# Revit family: TMS-Luna-Pendant
name_source: partatom
category: Lighting Fixtures
units: mm (PartAtom-declared; Revit-internal decimal feet)

## family parameters
Cut with Voids When Loaded = No
Host = Face
Light Source = No
Part Type = Normal
Room Calculation Point = No
Round Connector Dimension = Use Diameter
Shared = No

## types (18) — shared parameters
Apparent Load = 0 VA
Assembly Code = D5020200
Cable Material = Steel ASTM A53
Canopy Diameter = 0' - 10"
Canopy Material = TMS Gloss Black
Default Elevation = 4' - 0"
Fixture Material = TMS Gloss Black
Lens Material = TMS Lens
Manufacturer = TMS Lighting Inc.
Model = LUNA PENDANT
Number of Poles = 1
Power Factor = 1
URL = https://tmslighting.com
Voltage = 0 V

## per-type parameters (varying)
| type | Fixture Type | Number of Supports | Radius |
| 24" Direct | Luna-Fixture : 24" | 3 | 0' - 11 1/2" |
| 36" Direct | Luna-Fixture : 36" | 3 | 1' - 5 1/2" |
| 48" Direct | Luna-Fixture : 48" | 3 | 1' - 11 1/2" |
| 60" Direct | Luna-Fixture : 60" | 3 | 2' - 5 1/2" |
| 72" Direct | Luna-Fixture : 72" | 4 | 2' - 11 1/2" |
| 84" Direct | Luna-Fixture : 84" | 4 | 3' - 5 1/2" |
| 24" Direct/Indirect | Luna-Fixture-Dir-Ind : 24" | 3 | 0' - 11 1/2" |
| 36" Direct/Indirect | Luna-Fixture-Dir-Ind : 36" | 3 | 1' - 5 1/2" |
| 48" Direct/Indirect | Luna-Fixture-Dir-Ind : 48" | 3 | 1' - 11 1/2" |
| 60" Direct/Indirect | Luna-Fixture-Dir-Ind : 60" | 3 | 2' - 5 1/2" |
| 72" Direct/Indirect | Luna-Fixture-Dir-Ind : 72" | 4 | 2' - 11 1/2" |
| 84" Direct/Indirect | Luna-Fixture-Dir-Ind : 84" | 4 | 3' - 5 1/2" |
| 96" Direct/Indirect | Luna-Fixture-Dir-Ind : 96" | 8 | 3' - 11 1/2" |
| 120" Direct/Indirect | Luna-Fixture-Dir-Ind : 120" | 8 | 4' - 11 1/2" |
| 144" Direct/Indirect | Luna-Fixture-Dir-Ind : 144" | 8 | 5' - 11 1/2" |
| 96" Direct | Luna-Fixture : 96" | 8 | 3' - 11 1/2" |
| 120" Direct | Luna-Fixture : 120" | 8 | 4' - 11 1/2" |
| 144" Direct | Luna-Fixture : 144" | 8 | 5' - 11 1/2" |

## geometry (parser evidence)
native form markers: Sweep x28
no freeform markers — native parametric forms only
